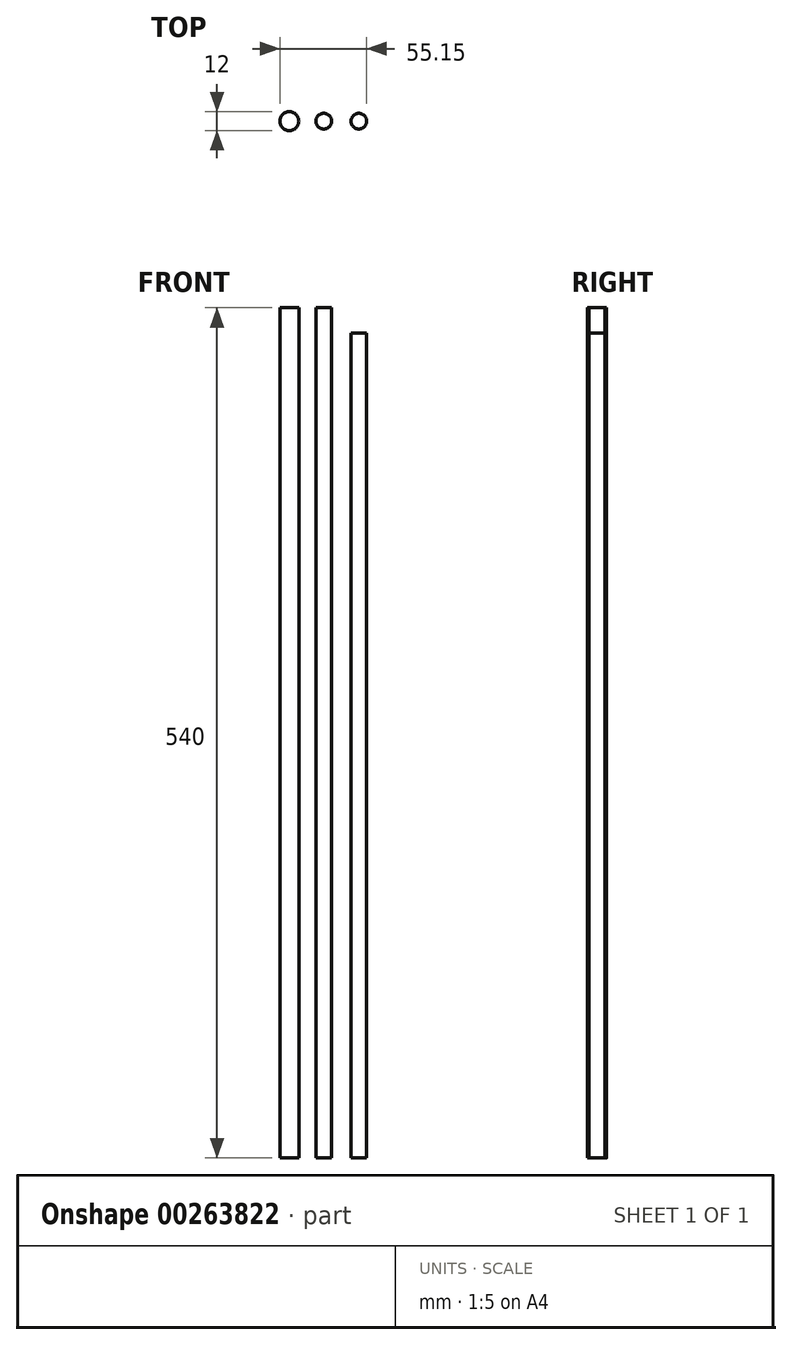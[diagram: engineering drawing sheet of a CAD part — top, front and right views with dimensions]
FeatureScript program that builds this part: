
annotation { "Feature Type Name" : "Feature", "Feature Type Description" : "" }
export const myFeature = defineFeature(function(context is Context, id is Id, definition is map)
    precondition{}
    {
        {
            var Q0;
            Q0=qCreatedBy(makeId("Top.planeOp"),FACE);
            var sketch = newSketch(context, id + "F0", { "sketchPlane" : qUnion([Q0])});
            skCircle(sketch, "E0", {"center": v(0, 0) * mm, "radius": 5 * mm});
            skSolve(sketch);
        }
        {
            var Q0;
            Q0=qSketchRegion(id+"F0",true);
            extrude(context, id + "F1", {"entities" : qUnion([Q0]), "depth" : 540 * mm});
        }
        {
            var Q0;
            Q0=qCreatedBy(makeId("Top.planeOp"),FACE);
            var sketch = newSketch(context, id + "F2", { "sketchPlane" : qUnion([Q0])});
            skCircle(sketch, "E1", {"center": v(22.28, 0) * mm, "radius": 5 * mm});
            skSolve(sketch);
        }
        {
            var Q0;
            Q0=qSketchRegion(id+"F2",true);
            extrude(context, id + "F3", {"entities" : qUnion([Q0]), "depth" : 524 * mm});
        }
        {
            var Q0;
            Q0=qCreatedBy(makeId("Top.planeOp"),FACE);
            var sketch = newSketch(context, id + "F4", { "sketchPlane" : qUnion([Q0])});
            skCircle(sketch, "E2", {"center": v(-21.87, 0) * mm, "radius": 6 * mm});
            skSolve(sketch);
        }
        {
            var Q0;
            Q0=qSketchRegion(id+"F4",true);
            extrude(context, id + "F5", {"entities" : qUnion([Q0]), "depth" : 540 * mm});
        }
    });
